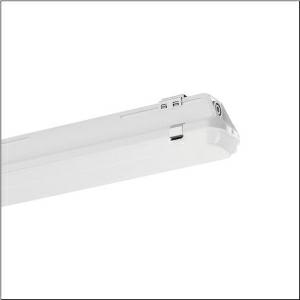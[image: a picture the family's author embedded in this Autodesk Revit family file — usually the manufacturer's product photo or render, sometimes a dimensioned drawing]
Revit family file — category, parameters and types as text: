
# Revit family: monsun_r__21_51fb20dl420k_b509
name_source: partatom
category: Lighting Fixtures
units: mm (PartAtom-declared; Revit-internal decimal feet)

## family parameters
Cut with Voids When Loaded = No
Host = Face
Light Source = No
Part Type = Normal
Room Calculation Point = No
Round Connector Dimension = Use Diameter
Shared = No

## types (1)
- --- (1 x LED, 2660 lm, 17.1 W, 4000K)
    Apparent Load = 17 VA
    CIE Flux Codes = 45 75 93 94 100
    Color Rendering = 80
    Color Temperature = 4000K
    Default Elevation = 1800 mm
    Description = Monsun® 21, damp-proof luminaire, chain hanger, primary optical cover: enclosure, of PC, light emission: direct distribution, primary light characteristic: symmetric, installation type: suspended mounting, surface-mounted, horizontal mounting, vertical mounting, LED, rated luminous flux: 2.660lm, luminous efficacy: 156lm/W, light colour: 840, colour temperature: 4000K, control gear: DALI 2, with terminal, 5-pole, max. 2.5mm², mains connection: 220..240V, AC, 50/60Hz, rated input power: 17W, housing, of glass-fibre reinforced plastic, uncoated, bright grey, incl. chain hanger, length: 1.299mm, width: 90mm, height: 88mm, clip for enclosure, of stainless steel (V2A), ceiling mounting element, of stainless steel (V2A), chain hanger, of stainless steel (V2A), protection rating (complete): IP66, insulation class (complete): insulation class I (protective earthing), certification: CE, ENEC, VDE, UKCA, protection symbol: D, impact resistance: IK08, permissible operating ambient temperature: -25..+35°C, standard: EN 50419, EN 60598-2-1, corresponds to IFS (International Featured Standards) requirements for safety and quality in the food industry, for indoor or canopied outdoor use, no direct snow, no direct sun, no direct rain, LABS conformity tested according to VDMA 24364:2018-05, contact your sales advisor before using the luminaires in applications with unclear chemical exposure, large temperature fluctuations or condensation-forming humidity, packaging unit: 1 piece
    Height = 88 mm
    Lamp = 1 x LED
    Lamp Light Flux = 2660 lm
    Lamp Power = 17.1 W
    Lamp count = 1
    Length = 1299 mm
    Luminous efficacy = 156 lm/W
    Manufacturer = Siteco
    ModVariant = No
    Model = 51FB20DL420K
    Mounting Place = Ceiling
    Mounting Type = Surface mounted
    Number of Poles = 1
    OnlyDefault = Yes
    Power Factor = 1
    Product Name = Monsun® 21
    Product group = damp-proof luminaire
    ProductGroupID = 300
    Protection Class = Protection class I
    Protection Degree = IP 66
    RLX_Detail_Level = 1
    RLX_Emergency_Light_Flux = 0 lm
    RLX_Emergency_Type = 0
    RLX_Emergency_Type_DB = No
    RlxData = <blob elided: 93093 chars, md5=b7b657bc>
    Socket = socket
    Standby Power = 0 W
    System Light Flux = 2660 lm
    System Power = 17 W
    Type Comments = factory setting: luminous flux: 100 % | dim-lin: 254 | 110 mA
    Type Image = l_1319656.jpg
    URL = http://relux.com
    VarID = @adj_022324
    Voltage = 0 V
    Weight = 0.00 kg
    Width = 90 mm

## geometry (parser evidence)
native form markers: Blend x4, Sweep x12
no freeform markers — native parametric forms only
